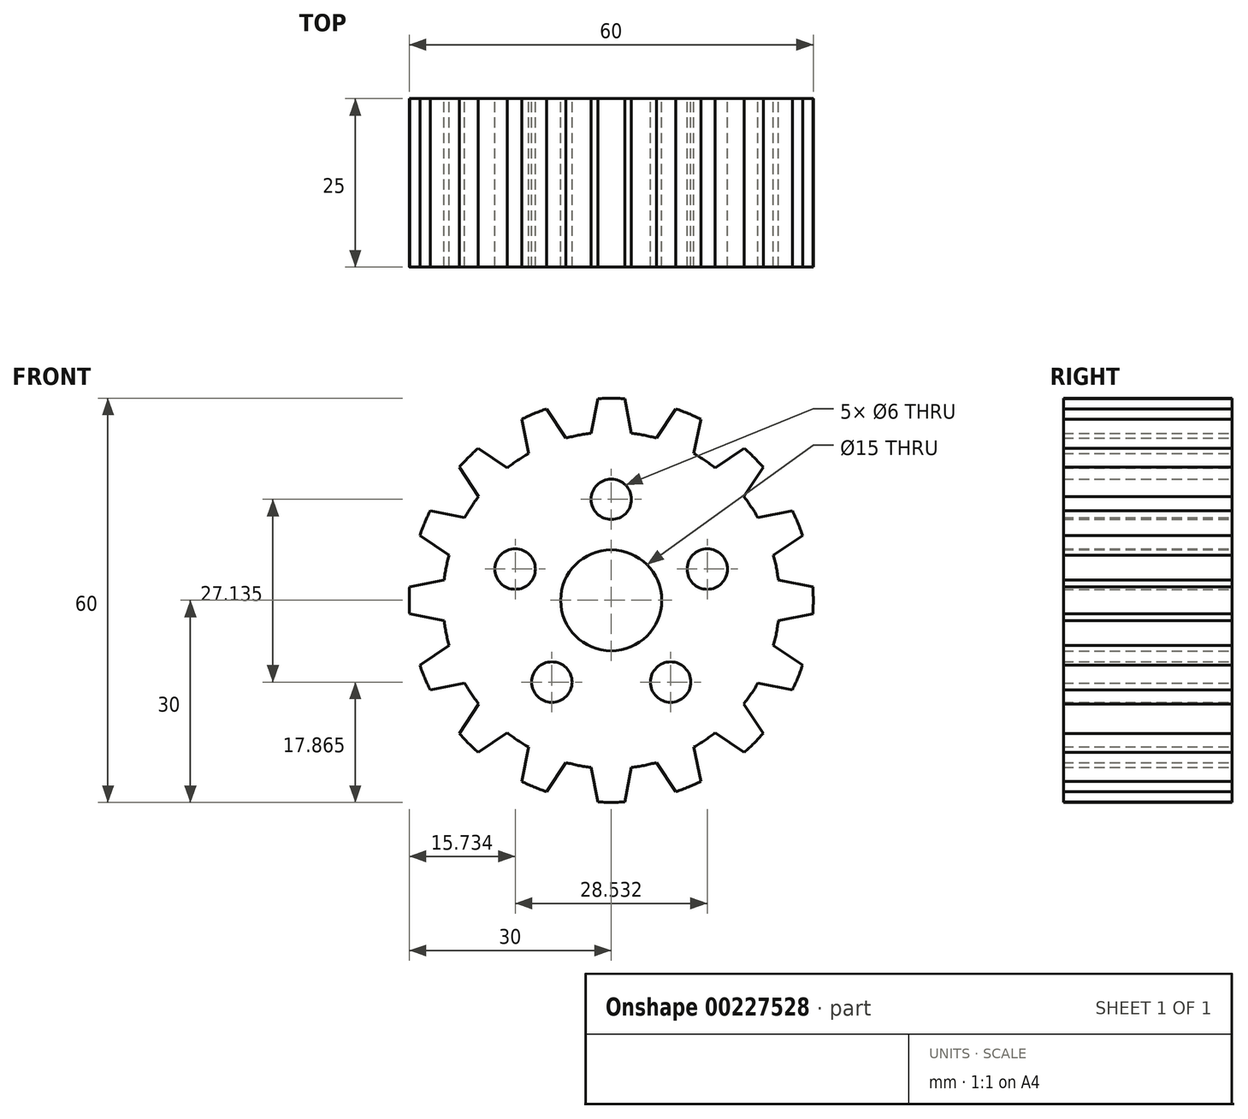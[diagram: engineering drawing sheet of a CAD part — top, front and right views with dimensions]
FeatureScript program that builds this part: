
annotation { "Feature Type Name" : "Feature", "Feature Type Description" : "" }
export const myFeature = defineFeature(function(context is Context, id is Id, definition is map)
    precondition{}
    {
        {
            var Q0;
            Q0=qCreatedBy(makeId("Front.planeOp"),FACE);
            var sketch = newSketch(context, id + "F0", { "sketchPlane" : qUnion([Q0])});
            skCircle(sketch, "E0", {"center": v(0, 0) * mm, "radius": 7.5 * mm});
            skCircle(sketch, "E1", {"center": v(0, 0) * mm, "radius": 15 * mm, "construction": true});
            skCircle(sketch, "E2", {"center": v(0, 0) * mm, "radius": 25 * mm});
            skArc(sketch, "E3", {"start": v(2, 29.93) * mm, "mid": v(0, 30) * mm, "end": v(-2, 29.93) * mm});
            skLineSegment(sketch, "E4", {"start": v(-2, 29.93) * mm, "end": v(-3, 24.82) * mm});
            skLineSegment(sketch, "E5", {"start": v(2, 29.93) * mm, "end": v(3, 24.82) * mm});
            skLineSegment(sketch, "E6", {"start": v(0, 39.1) * mm, "end": v(0, 10.33) * mm, "construction": true});
            skLineSegment(sketch, "E7.1.0", {"start": v(-13.3, 26.89) * mm, "end": v(-12.27, 21.78) * mm});
            skArc(sketch, "E7.1.1", {"start": v(-9.6, 28.42) * mm, "mid": v(-11.48, 27.72) * mm, "end": v(-13.3, 26.89) * mm});
            skLineSegment(sketch, "E7.1.2", {"start": v(-9.6, 28.42) * mm, "end": v(-6.73, 24.08) * mm});
            skLineSegment(sketch, "E7.2.0", {"start": v(-22.58, 19.75) * mm, "end": v(-19.67, 15.43) * mm});
            skArc(sketch, "E7.2.1", {"start": v(-19.75, 22.58) * mm, "mid": v(-21.21, 21.21) * mm, "end": v(-22.58, 19.75) * mm});
            skLineSegment(sketch, "E7.2.2", {"start": v(-19.75, 22.58) * mm, "end": v(-15.43, 19.67) * mm});
            skLineSegment(sketch, "E7.3.0", {"start": v(-28.42, 9.6) * mm, "end": v(-24.08, 6.73) * mm});
            skArc(sketch, "E7.3.1", {"start": v(-26.89, 13.3) * mm, "mid": v(-27.72, 11.48) * mm, "end": v(-28.42, 9.6) * mm});
            skLineSegment(sketch, "E7.3.2", {"start": v(-26.89, 13.3) * mm, "end": v(-21.78, 12.27) * mm});
            skLineSegment(sketch, "E7.4.0", {"start": v(-29.93, -2) * mm, "end": v(-24.82, -3) * mm});
            skArc(sketch, "E7.4.1", {"start": v(-29.93, 2) * mm, "mid": v(-30, 0) * mm, "end": v(-29.93, -2) * mm});
            skLineSegment(sketch, "E7.4.2", {"start": v(-29.93, 2) * mm, "end": v(-24.82, 3) * mm});
            skLineSegment(sketch, "E7.5.0", {"start": v(-26.89, -13.3) * mm, "end": v(-21.78, -12.27) * mm});
            skArc(sketch, "E7.5.1", {"start": v(-28.42, -9.6) * mm, "mid": v(-27.72, -11.48) * mm, "end": v(-26.89, -13.3) * mm});
            skLineSegment(sketch, "E7.5.2", {"start": v(-28.42, -9.6) * mm, "end": v(-24.08, -6.73) * mm});
            skLineSegment(sketch, "E7.6.0", {"start": v(-19.75, -22.58) * mm, "end": v(-15.43, -19.67) * mm});
            skArc(sketch, "E7.6.1", {"start": v(-22.58, -19.75) * mm, "mid": v(-21.21, -21.21) * mm, "end": v(-19.75, -22.58) * mm});
            skLineSegment(sketch, "E7.6.2", {"start": v(-22.58, -19.75) * mm, "end": v(-19.67, -15.43) * mm});
            skLineSegment(sketch, "E7.7.0", {"start": v(-9.6, -28.42) * mm, "end": v(-6.73, -24.08) * mm});
            skArc(sketch, "E7.7.1", {"start": v(-13.3, -26.89) * mm, "mid": v(-11.48, -27.72) * mm, "end": v(-9.6, -28.42) * mm});
            skLineSegment(sketch, "E7.7.2", {"start": v(-13.3, -26.89) * mm, "end": v(-12.27, -21.78) * mm});
            skLineSegment(sketch, "E7.8.0", {"start": v(2, -29.93) * mm, "end": v(3, -24.82) * mm});
            skArc(sketch, "E7.8.1", {"start": v(-2, -29.93) * mm, "mid": v(0, -30) * mm, "end": v(2, -29.93) * mm});
            skLineSegment(sketch, "E7.8.2", {"start": v(-2, -29.93) * mm, "end": v(-3, -24.82) * mm});
            skLineSegment(sketch, "E7.9.0", {"start": v(13.3, -26.89) * mm, "end": v(12.27, -21.78) * mm});
            skArc(sketch, "E7.9.1", {"start": v(9.6, -28.42) * mm, "mid": v(11.48, -27.72) * mm, "end": v(13.3, -26.89) * mm});
            skLineSegment(sketch, "E7.9.2", {"start": v(9.6, -28.42) * mm, "end": v(6.73, -24.08) * mm});
            skLineSegment(sketch, "E7.10.0", {"start": v(22.58, -19.75) * mm, "end": v(19.67, -15.43) * mm});
            skArc(sketch, "E7.10.1", {"start": v(19.75, -22.58) * mm, "mid": v(21.21, -21.21) * mm, "end": v(22.58, -19.75) * mm});
            skLineSegment(sketch, "E7.10.2", {"start": v(19.75, -22.58) * mm, "end": v(15.43, -19.67) * mm});
            skLineSegment(sketch, "E7.11.0", {"start": v(28.42, -9.6) * mm, "end": v(24.08, -6.73) * mm});
            skArc(sketch, "E7.11.1", {"start": v(26.89, -13.3) * mm, "mid": v(27.72, -11.48) * mm, "end": v(28.42, -9.6) * mm});
            skLineSegment(sketch, "E7.11.2", {"start": v(26.89, -13.3) * mm, "end": v(21.78, -12.27) * mm});
            skLineSegment(sketch, "E7.12.0", {"start": v(29.93, 2) * mm, "end": v(24.82, 3) * mm});
            skArc(sketch, "E7.12.1", {"start": v(29.93, -2) * mm, "mid": v(30, 0) * mm, "end": v(29.93, 2) * mm});
            skLineSegment(sketch, "E7.12.2", {"start": v(29.93, -2) * mm, "end": v(24.82, -3) * mm});
            skLineSegment(sketch, "E7.13.0", {"start": v(26.89, 13.3) * mm, "end": v(21.78, 12.27) * mm});
            skArc(sketch, "E7.13.1", {"start": v(28.42, 9.6) * mm, "mid": v(27.72, 11.48) * mm, "end": v(26.89, 13.3) * mm});
            skLineSegment(sketch, "E7.13.2", {"start": v(28.42, 9.6) * mm, "end": v(24.08, 6.73) * mm});
            skLineSegment(sketch, "E7.14.0", {"start": v(19.75, 22.58) * mm, "end": v(15.43, 19.67) * mm});
            skArc(sketch, "E7.14.1", {"start": v(22.58, 19.75) * mm, "mid": v(21.21, 21.21) * mm, "end": v(19.75, 22.58) * mm});
            skLineSegment(sketch, "E7.14.2", {"start": v(22.58, 19.75) * mm, "end": v(19.67, 15.43) * mm});
            skLineSegment(sketch, "E7.15.0", {"start": v(9.6, 28.42) * mm, "end": v(6.73, 24.08) * mm});
            skArc(sketch, "E7.15.1", {"start": v(13.3, 26.89) * mm, "mid": v(11.48, 27.72) * mm, "end": v(9.6, 28.42) * mm});
            skLineSegment(sketch, "E7.15.2", {"start": v(13.3, 26.89) * mm, "end": v(12.27, 21.78) * mm});
            skCircle(sketch, "E8", {"center": v(0, 15) * mm, "radius": 3 * mm});
            skCircle(sketch, "E9.1.0", {"center": v(-14.27, 4.64) * mm, "radius": 3 * mm});
            skCircle(sketch, "E9.2.0", {"center": v(-8.82, -12.14) * mm, "radius": 3 * mm});
            skCircle(sketch, "E9.3.0", {"center": v(8.82, -12.14) * mm, "radius": 3 * mm});
            skCircle(sketch, "E9.4.0", {"center": v(14.27, 4.64) * mm, "radius": 3 * mm});
            skSolve(sketch);
        }
        {
            var Q0;
            Q0 = qSketchRegion(id + "F0", true);
            var Q1;
            Q1=makeQuery(id+"F0.imprint","IMPRINT",FACE,{"disambiguationData":[TD([[makeQuery(id+"F0.imprint","IMPRINT",EDGE,{"derivedFrom":sQuery(id+"F0.wireOp",EDGE,"E0")}),-1.0]])]});
            extrude(context, id + "F1", {"entities" : qUnion([Q0, Q1]), "depth" : 25 * mm});
        }
    });
